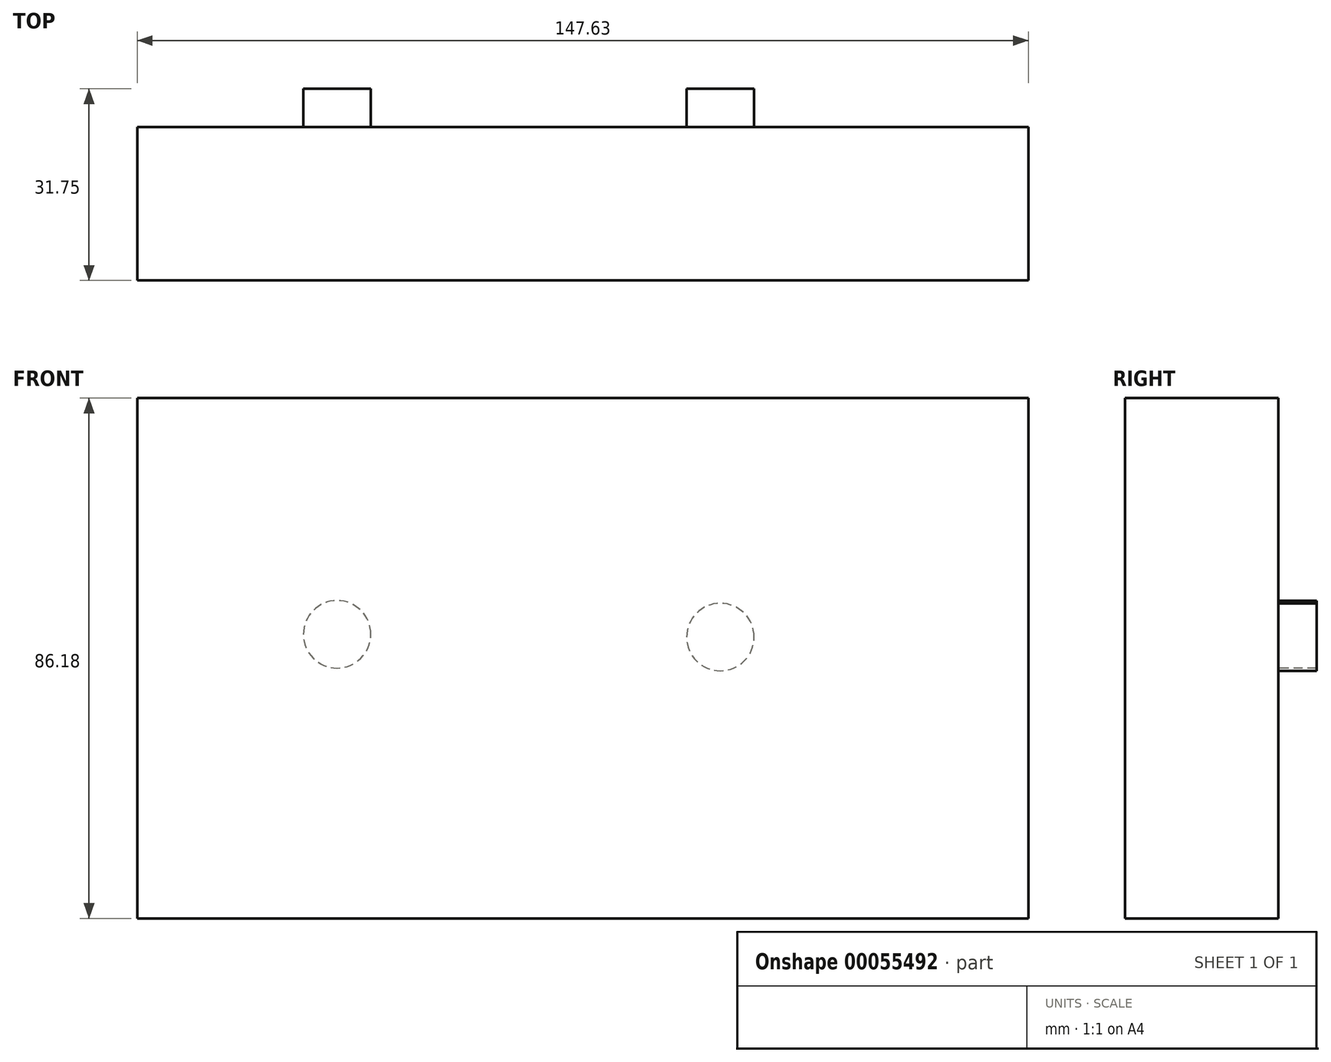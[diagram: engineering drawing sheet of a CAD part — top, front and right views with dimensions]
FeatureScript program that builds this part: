
annotation { "Feature Type Name" : "Feature", "Feature Type Description" : "" }
export const myFeature = defineFeature(function(context is Context, id is Id, definition is map)
    precondition{}
    {
        {
            var Q0;
            Q0=qCreatedBy(makeId("Front.planeOp"),FACE);
            var sketch = newSketch(context, id + "F0", { "sketchPlane" : qUnion([Q0])});
            skLineSegment(sketch, "E0.bottom", {"start": v(-53.82, -19.29) * mm, "end": v(68.41, -19.29) * mm});
            skLineSegment(sketch, "E0.top", {"start": v(-53.82, 66.89) * mm, "end": v(68.41, 66.89) * mm});
            skLineSegment(sketch, "E0.left", {"start": v(-53.82, -19.29) * mm, "end": v(-53.82, 66.89) * mm});
            skLineSegment(sketch, "E0.right", {"start": v(68.41, -19.29) * mm, "end": v(68.41, 66.89) * mm});
            skLineSegment(sketch, "E1", {"start": v(42.79, 61.9) * mm, "end": v(42.79, -7.27) * mm, "construction": true});
            skLineSegment(sketch, "E2", {"start": v(-20.71, 62.8) * mm, "end": v(-20.71, -7.27) * mm, "construction": true});
            skCircle(sketch, "E3", {"center": v(42.79, 27.31) * mm, "radius": 5.59 * mm});
            skCircle(sketch, "E4", {"center": v(-20.71, 27.77) * mm, "radius": 5.59 * mm});
            skSolve(sketch);
        }
        {
            var Q0;
            Q0 = qSketchRegion(id + "F0", true);
            var Q1;
            Q1=makeQuery(id+"F0.imprint","IMPRINT",FACE,{"disambiguationData":[TD([[makeQuery(id+"F0.imprint","IMPRINT",EDGE,{"derivedFrom":sQuery(id+"F0.wireOp",EDGE,"E3")}),1.0]])]});
            var Q2;
            Q2=makeQuery(id+"F0.imprint","IMPRINT",FACE,{"disambiguationData":[TD([[makeQuery(id+"F0.imprint","IMPRINT",EDGE,{"derivedFrom":sQuery(id+"F0.wireOp",EDGE,"E4")}),1.0]])]});
            extrude(context, id + "F1", {"entities" : qUnion([Q0, Q1, Q2]), "depth" : 25.4 * mm});
        }
        {
            var Q0;
            Q0=makeQuery(id+"F0.imprint","IMPRINT",FACE,{"disambiguationData":[TD([[makeQuery(id+"F0.imprint","IMPRINT",EDGE,{"derivedFrom":sQuery(id+"F0.wireOp",EDGE,"E3")}),1.0]])]});
            var Q1;
            Q1=makeQuery(id+"F0.imprint","IMPRINT",FACE,{"disambiguationData":[TD([[makeQuery(id+"F0.imprint","IMPRINT",EDGE,{"derivedFrom":sQuery(id+"F0.wireOp",EDGE,"E4")}),1.0]])]});
            extrude(context, id + "F2", {"entities" : qUnion([Q0, Q1]), "operationType" : NewBodyOperationType.ADD, "oppositeDirection" : true, "depth" : 6.35 * mm});
        }
        {
            var Q0;
            Q0=makeQuery(id+"F1.opExtrude","SWEPT_FACE",FACE,{"disambiguationData":[OSD([sQuery(id+"F0.wireOp",EDGE,"E0.right")])]});
            extrude(context, id + "F3", {"entities" : qUnion([Q0]), "operationType" : NewBodyOperationType.ADD, "depth" : 25.4 * mm});
        }
    });
